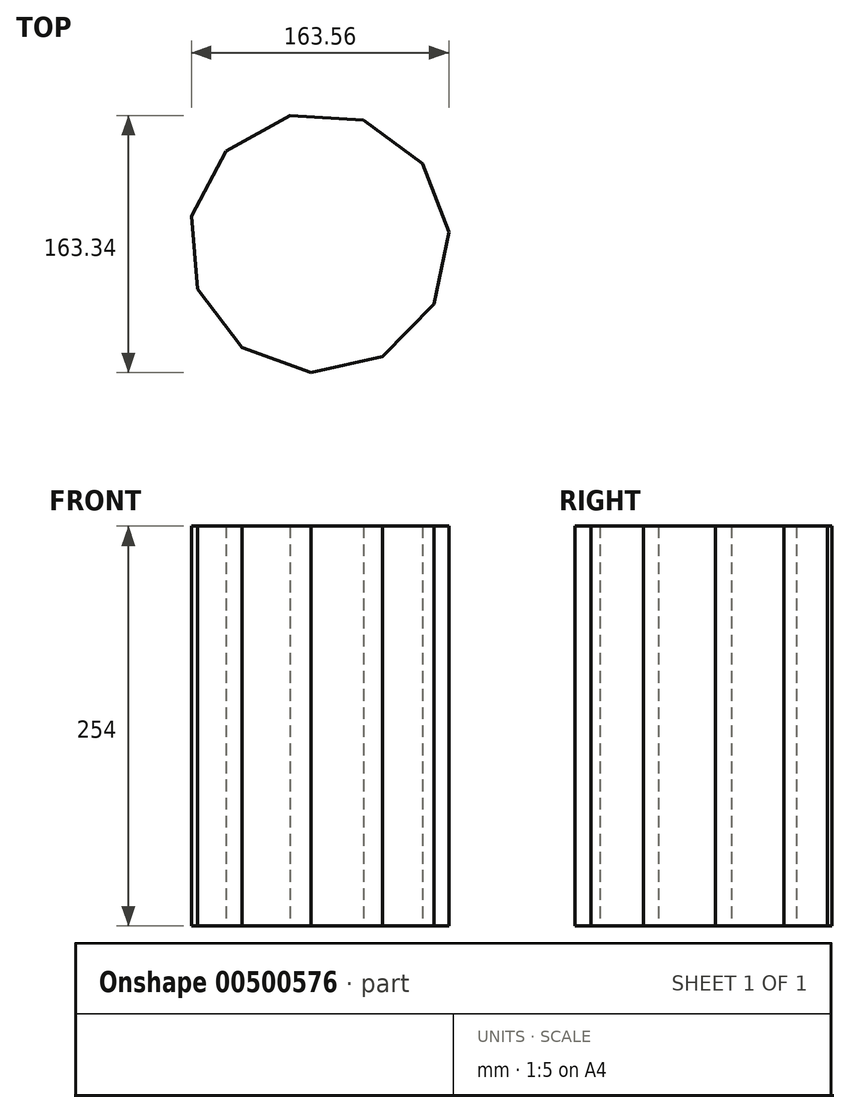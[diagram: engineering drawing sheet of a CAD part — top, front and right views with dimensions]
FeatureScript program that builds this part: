
annotation { "Feature Type Name" : "Feature", "Feature Type Description" : "" }
export const myFeature = defineFeature(function(context is Context, id is Id, definition is map)
    precondition{}
    {
        {
            var Q0;
            Q0=qCreatedBy(makeId("Top.planeOp"),FACE);
            var sketch = newSketch(context, id + "F0", { "sketchPlane" : qUnion([Q0])});
            skPoint(sketch, "E0", {"position": v(-6.71, 0) * mm});
            skCircle(sketch, "E1.cCircle", {"center": v(-6.71, 0) * mm, "radius": 82.78 * mm, "construction": true});
            skLineSegment(sketch, "E1.0", {"start": v(-65.78, 58) * mm, "end": v(-25.05, 80.72) * mm});
            skLineSegment(sketch, "E1.1", {"start": v(-25.05, 80.72) * mm, "end": v(21.5, 77.82) * mm});
            skLineSegment(sketch, "E1.2", {"start": v(21.5, 77.82) * mm, "end": v(59.1, 50.21) * mm});
            skLineSegment(sketch, "E1.3", {"start": v(59.1, 50.21) * mm, "end": v(75.8, 6.66) * mm});
            skLineSegment(sketch, "E1.4", {"start": v(75.8, 6.66) * mm, "end": v(66.3, -39) * mm});
            skLineSegment(sketch, "E1.5", {"start": v(66.3, -39) * mm, "end": v(33.62, -72.29) * mm});
            skLineSegment(sketch, "E1.6", {"start": v(33.62, -72.29) * mm, "end": v(-11.86, -82.62) * mm});
            skLineSegment(sketch, "E1.7", {"start": v(-11.86, -82.62) * mm, "end": v(-55.7, -66.72) * mm});
            skLineSegment(sketch, "E1.8", {"start": v(-55.7, -66.72) * mm, "end": v(-84, -29.64) * mm});
            skLineSegment(sketch, "E1.9", {"start": v(-84, -29.64) * mm, "end": v(-87.76, 16.85) * mm});
            skLineSegment(sketch, "E1.10", {"start": v(-87.76, 16.85) * mm, "end": v(-65.78, 58) * mm});
            skSolve(sketch);
        }
        {
            var Q0;
            Q0=makeQuery(id+"F0.imprint","IMPRINT",FACE,{"disambiguationData":[TD([[makeQuery(id+"F0.imprint","IMPRINT",EDGE,{"derivedFrom":sQuery(id+"F0.wireOp",EDGE,"E1.0")}),-1.0]])]});
            extrude(context, id + "F1", {"entities" : qUnion([Q0]), "depth" : 254 * mm});
        }
    });
